# Revit family: KS ALU-PU 80 -s-, DS 40, M 8-M10, Ø 17,2
name_source: partatom
category: HLS-Bauteile
revit_build: Autodesk Revit 2017 (Build: 20190507_1515(x64)
units: mm (PartAtom-declared; Revit-internal decimal feet)

## family parameters
Arbeitsebenenbasiert = Ja
Beim Laden mit Abzugskörper schneiden = Nein
Bemaßung runder Anschluss = Durchmesser verwenden
Gemeinsam genutzt = Ja
Immer vertikal = Nein
Raumberechnungspunkt = Nein
Teiletyp = Normal

## types (1)
- Kälteschelle ALU-PU 80 -s-, DS 40, M8/M10, Ø 17,2
    A = 58 mm  [stored 0.190289 ft]
    Anschluss = M8/M10
    Anschlußhöhe = 58 mm
    Artikelnummer = 71401848
    B = 134 mm  [stored 0.439633 ft]
    Baustoffklasse = B2
    Breite = 141 mm
    D = 18 mm  [stored 0.0590551 ft]
    D0 = 98 mm  [stored 0.321522 ft]
    DF1 = 16 mm  [stored 0.0524934 ft]
    DF2 = 16 mm  [stored 0.0524934 ft]
    DS = 40 mm  [stored 0.131234 ft]
    DVS = 5 mm  [stored 0.0164042 ft]
    Dichte Kern = 80 kg/m³
    Dichte Mantel = 2.700 kg/m³
    Dicke Mantel = 0,08 mm
    Dämmkörper = ALU/PU
    Dämmstärke = 40 mm  [stored 0.131234 ft]
    EAN = 4250928441683
    Fabrikat = MEFA
    Firma = MEFA Befestigungs- und Montagesysteme GmbH
    Gewicht = 0.19 kg
    Gewicht pro Bauteil = 0.19 kg
    H = 118 mm  [stored 0.387139 ft]
    H1 = 2 mm  [stored 0.00656168 ft]
    H2 = 4 mm  [stored 0.0131234 ft]
    HGA = 16 mm  [stored 0.0524934 ft]
    Kurztext1 = Kälteschelle RG80s ALU/PU
    Kurztext2 = 17,2 mm Iso 40 x 40 mm M8/M10
    L = 40 mm  [stored 0.131234 ft]
    MB = 25 mm  [stored 0.082021 ft]
    MD = 2 mm  [stored 0.00656168 ft]
    Material = Stahl
    Material Mantel = Alufolie
    Materialname = DD11
    Mengeneinheit = St
    Oberflaeche = galvanisch verzinkt
    R = 49 mm  [stored 0.160761 ft]
    RM = 51 mm
    Rohraußendurchmesser Kupfer = 18 mm
    Rohraußendurchmesser Stahl = 17,2 mm
    Rohrschellentyp = Trabant
    S = 118 mm  [stored 0.387139 ft]
    Schalenlänge = 40 mm
    Vorgabe-Ansicht = 1219 mm
    Wasserdampfdiffusionswiderstand = 18750 µ
    Wärmeleitfähigkeit = 0.025 W/mK
    max. Temperaturbeständigkeit = 120 °C
    max. zul. Last = 0.10 kN
    mittl. Nenndruckfestigkeit Kern = 0,5 N/mm²
    stat. Belastung Kern = 0,1 N/mm²
    vpe = 1 St

note: [stored X ft] marks values corroborated as IEEE doubles in the binary element streams (Revit-internal decimal feet)

## geometry (parser evidence)
native form markers: Sweep x2
no freeform markers — native parametric forms only
